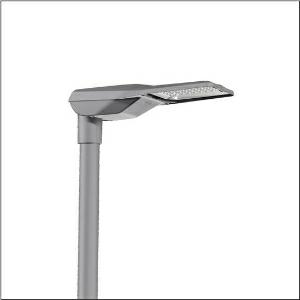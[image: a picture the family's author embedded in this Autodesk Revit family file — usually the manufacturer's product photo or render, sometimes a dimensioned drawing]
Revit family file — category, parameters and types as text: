
# Revit family: streetlight_sl_21_iq_mini___st0_5a_5xe2b41d08jb_1bd7
name_source: partatom
category: Lighting Fixtures
units: mm (PartAtom-declared; Revit-internal decimal feet)

## family parameters
Cut with Voids When Loaded = No
Host = Face
Light Source = No
Part Type = Normal
Room Calculation Point = No
Round Connector Dimension = Use Diameter
Shared = No

## types (1)
- --- (1 x LED, 11290 lm, 71.6 W, 4000K)
    Apparent Load = 72 VA
    CIE Flux Codes = 43 76 97 100 100
    Color Rendering = 70
    Color Temperature = 4000K
    Default Elevation = 1800 mm
    Description = Streetlight SL 21 mini, mast luminaire, primary light control with lens, of PMMA, primary optical cover: cover, of toughened safety glass, transparent, light distribution: ST0.5a, light emission: direct distribution, primary light characteristic: asymmetric, installation type: post-top, side-entry, LED, High Power LED, rated luminous flux: 11.290lm, luminous efficacy: 158lm/W, light colour: 740, colour temperature: 4000K, control gear: ECG iQ, control: Auto-Match, Temp-Guard, Lumen-Switch, Night-Set, Smart-Wire, Light-Fading, Desk-Remote (wireless, voltage-free reading and setting of iQ features in the workshop via application-optimized NFC function/RFID function), optimised constant luminous flux control (CLO 2.0), mains connection: 220..240V, AC, 50/60Hz, start of lifetime: 72W, end of lifetime: 75W, reduction: 33W, luminaire housing, of diecast aluminium, powder-coated, Siteco® metallic grey (DB 702S), corrosivity category C5 according to DIN EN ISO 12944, length: 628mm, width: 235mm, height: 110mm, spigot size: 60/76mm (post-top) and 42/60/76mm (side-entry), mast flange for spigot size: 42mm: 5XC10008XM4, 60mm: 5XC10008XM2, 76/60mm: 5XC10108XM1, protection rating (complete): IP66, insulation class (complete): insulation class II (safety insulation), certification: CE, ENEC, VDE, impact resistance: IK09, permissible operating ambient temperature for outdoor applications: -40..+50°C, standard-compliant lighting for roads and squares, packaging unit: 1 piece

Light Distribution: ST0.5a
    Height = 110 mm
    Lamp = 1 x LED
    Lamp Light Flux = 11290 lm
    Lamp Power = 71.6 W
    Lamp count = 1
    Length = 625 mm
    Luminous efficacy = 158 lm/W
    Manufacturer = Siteco
    ModVariant = No
    Model = 5XE2B41D08JB
    Number of Poles = 1
    OnlyDefault = Yes
    Power Factor = 1
    Product Name = Streetlight SL 21 iQ mini | ST0.5a
    Product group = mast luminaire | pylon top
    ProductGroupID = 6100
    Protection Class = Protection class II
    Protection Degree = IP 66
    RLX_Detail_Level = 1
    RlxData = <blob elided: 103157 chars, md5=4c94702e>
    Socket = socket
    Standby Power = 0 W
    System Light Flux = 11290 lm
    System Power = 72 W
    Type Comments = factory setting: luminous flux: 100 % | dim-lin: 254 | 746 mA
    Type Image = l_1003519.jpg
    URL = http://relux.com
    VarID = @adj_084133
    Voltage = 0 V
    Weight = 0.00 kg
    Width = 234 mm

## geometry (parser evidence)
native form markers: Blend x4, Sweep x11
no freeform markers — native parametric forms only
